# Revit family: VLGFL1991-7DAWSxxxBxxxx
name_source: partatom
category: Leuchten
units: mm (PartAtom-declared; Revit-internal decimal feet)

## family parameters
Basisbauteil = Fläche
Beim Laden mit Abzugskörper schneiden = Nein
Bemaßung runder Anschluss = Durchmesser verwenden
Gemeinsam genutzt = Nein
Lichtquelle = Ja
OmniClass-Nummer = 23.80.70.11
OmniClass-Titel = Luminaries for Internal Lighting
Raumberechnungspunkt = Nein
Teiletyp = Normal

## types (6) — shared parameters
Baugruppenkennzeichen = D5020200
Emissionsform beim Rendern sichtbar = Nein
Farbfilter = 16777215
Farbtemperaturverschiebung bei Dämpfen der Lampe = <Keine Auswahl>
Hersteller = RIDI Leuchten GmbH
Lampe = LED
Neigungswinkel = 90.00°
Scheinlast = 62 VA
URL = www.ridi.de
Von Breite des Rechtecks ausssenden = 1963 mm
Von Länge des Rechtecks aussenden = 29 mm  [stored 0.0951444 ft]
brand = RIDI
conformity mark = CE
electrical safety class = 1
height = 66 mm  [stored 0.216535 ft]
ingress protection (IP) code = IP54
length = 1994 mm  [stored 6.54199 ft]
nominal frequency = 50-60Hz
nominal voltage = 230
rated input power = 62
voltage type (AC, DC, UC) = AC
weight = 2,64
width = 67 mm
zero-valued in all types: Vorgabe-Ansicht

## per-type parameters (varying)
| type | Datei für fotometrisches Netz | Modell |
| VLGFL1991-7DAWS830B1000 | VLGFL1501-5NDWS840B0800.IES | 1561390 |
| VLGFL1991-7DAWS840B1100 | VLGFL1501-5NDWS840B0800.IES | 1561391 |
| VLGFL1991-7DAWS865B1100 | VLGFL1501-5NDWS840B0800.IES | 1561392 |
| VLGFL1991-7DAWS830E1100 | VLGFL1501-5NDWS840E0850.IES | 1561393 |
| VLGFL1991-7DAWS840E1100 | VLGFL1501-5NDWS840E0850.IES | 1561394 |
| VLGFL1991-7DAWS865E1100 | VLGFL1501-5NDWS840E0850.IES | 1561395 |

note: column(s) folded — value = type name in every type: product name

note: [stored X ft] marks values corroborated as IEEE doubles in the binary element streams (Revit-internal decimal feet)
